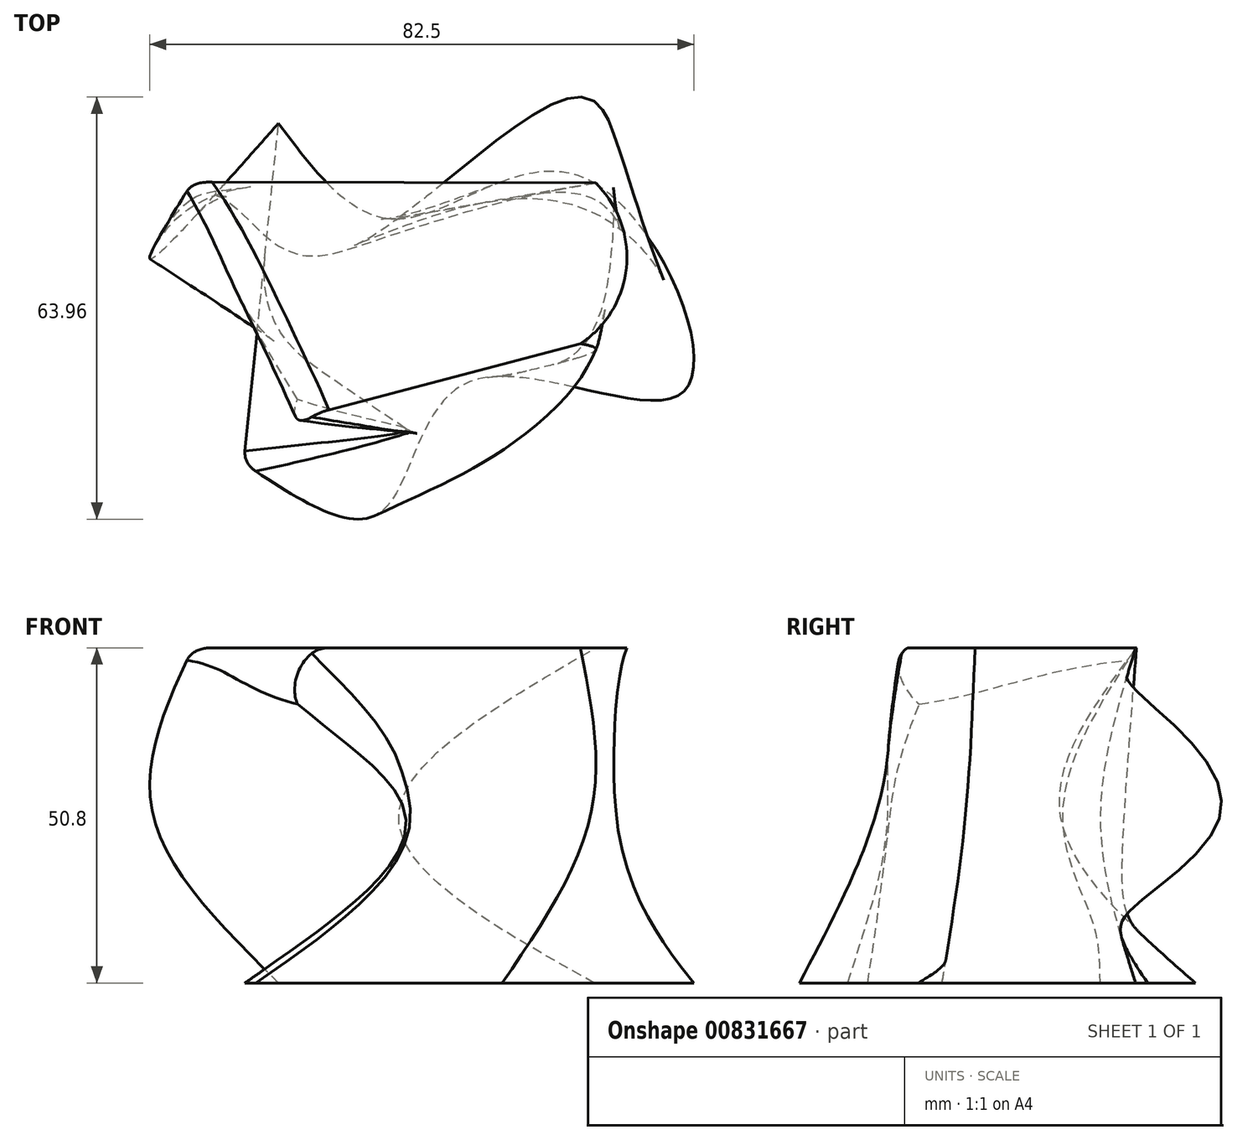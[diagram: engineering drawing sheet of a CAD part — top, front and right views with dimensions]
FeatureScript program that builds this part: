
annotation { "Feature Type Name" : "Feature", "Feature Type Description" : "" }
export const myFeature = defineFeature(function(context is Context, id is Id, definition is map)
    precondition{}
    {
        {
            var Q0;
            Q0=qCreatedBy(makeId("Top.planeOp"),FACE);
            cPlane(context, id + "F0", {"entities" : qUnion([Q0]), "cplaneType" : CPlaneType.OFFSET, "offset" : 25.4 * mm, "width" : 152.4 * mm, "height" : 152.4 * mm});
        }
        {
            var Q0;
            Q0=qCreatedBy(id+"F0.planeOp",FACE);
            cPlane(context, id + "F1", {"entities" : qUnion([Q0]), "cplaneType" : CPlaneType.OFFSET, "offset" : 25.4 * mm, "width" : 152.4 * mm, "height" : 152.4 * mm});
        }
        {
            var Q0;
            Q0=qCreatedBy(id+"F1.planeOp",FACE);
            var sketch = newSketch(context, id + "F2", { "sketchPlane" : qUnion([Q0])});
            skLineSegment(sketch, "E0", {"start": v(-26.46, -29.92) * mm, "end": v(27.37, -15.76) * mm});
            skArc(sketch, "E1", {"start": v(27.37, -15.76) * mm, "mid": v(34.34, -4.13) * mm, "end": v(29.67, 8.6) * mm});
            skArc(sketch, "E2", {"start": v(-26.46, -29.92) * mm, "mid": v(-24.66, -10.03) * mm, "end": v(-31.4, 8.77) * mm});
            skLineSegment(sketch, "E3", {"start": v(-31.4, 8.77) * mm, "end": v(29.67, 8.6) * mm});
            skSolve(sketch);
        }
        {
            var Q0;
            Q0=qCreatedBy(id+"F0.planeOp",FACE);
            var sketch = newSketch(context, id + "F3", { "sketchPlane" : qUnion([Q0])});
            skLineSegment(sketch, "E4", {"start": v(-37.4, -2.78) * mm, "end": v(1.19, -28.84) * mm});
            skFitSpline(sketch, "E5", {"points": [v(-37.4, -2.78) * mm, v(-28.18, 6.8) * mm, v(-19.66, 0) * mm, v(-5.19, 0) * mm, v(30.33, 20.18) * mm, v(28.9, -17.2) * mm], "startDerivative": vector(52.45, 134.23) * mm, "endDerivative": vector(-16.01, -12.86) * mm});
            skArc(sketch, "E6", {"start": v(1.19, -28.84) * mm, "mid": v(17.67, -29.26) * mm, "end": v(28.9, -17.2) * mm});
            skSolve(sketch);
        }
        {
            var Q0;
            Q0=qCreatedBy(makeId("Top.planeOp"),FACE);
            var sketch = newSketch(context, id + "F4", { "sketchPlane" : qUnion([Q0])});
            skLineSegment(sketch, "E7", {"start": v(-23.67, -33.87) * mm, "end": v(-18.4, 17.66) * mm});
            skFitSpline(sketch, "E8", {"points": [v(-18.4, 17.66) * mm, v(0, 3.17) * mm, v(27.86, 9.43) * mm, v(43.17, -22.84) * mm, v(10.58, -21.53) * mm, v(-2.92, -41.28) * mm, v(-23.67, -33.87) * mm], "startDerivative": vector(108.05, -144.99) * mm, "endDerivative": vector(-162.68, 108.74) * mm});
            skSolve(sketch);
        }
        {
            var Q0;
            Q0=makeQuery(id+"F4.imprint","IMPRINT",FACE,{"disambiguationData":[TD([[makeQuery(id+"F4.imprint","IMPRINT",EDGE,{"derivedFrom":sQuery(id+"F4.wireOp",EDGE,"E7")}),-1.0]])]});
            var Q1;
            Q1=makeQuery(id+"F3.imprint","IMPRINT",FACE,{"disambiguationData":[TD([[makeQuery(id+"F3.imprint","IMPRINT",EDGE,{"derivedFrom":sQuery(id+"F3.wireOp",EDGE,"E4")}),1.0]])]});
            var Q2;
            Q2=makeQuery(id+"F2.imprint","IMPRINT",FACE,{"disambiguationData":[TD([[makeQuery(id+"F2.imprint","IMPRINT",EDGE,{"derivedFrom":sQuery(id+"F2.wireOp",EDGE,"E0")}),1.0]])]});
            loft(context, id + "F5", {"sheetProfilesArray" : [{ "sheetProfileEntities" : qUnion([Q0]) }, { "sheetProfileEntities" : qUnion([Q1]) }, { "sheetProfileEntities" : qUnion([Q2]) }]});
        }
        {
            var Q0;
            Q0=makeQuery(id+"F5.opLoft","SWEPT_EDGE",EDGE,{"disambiguationData":[OSD([sQuery(id+"F2.wireOp",EDGE,"E0"),sQuery(id+"F2.wireOp",EDGE,"E2"),sQuery(id+"F3.wireOp",EDGE,"E4"),sQuery(id+"F3.wireOp",EDGE,"E6"),sQuery(id+"F4.wireOp",EDGE,"E7"),sQuery(id+"F4.wireOp",EDGE,"E8")])]});
            var Q1;
            Q1=makeQuery(id+"F5.opLoft","MID_CAP_EDGE",EDGE,{"disambiguationData":[OSD([sQuery(id+"F2.wireOp",EDGE,"E0"),sQuery(id+"F2.wireOp",EDGE,"E2"),sQuery(id+"F2.wireOp",EDGE,"E3")])],"capPos":2.0});
            fillet(context, id + "F6", {"entities" : qUnion([Q0, Q1]), "radius" : 5.08 * mm, "tangentPropagation" : true, "allowEdgeOverflow" : false});
        }
    });
